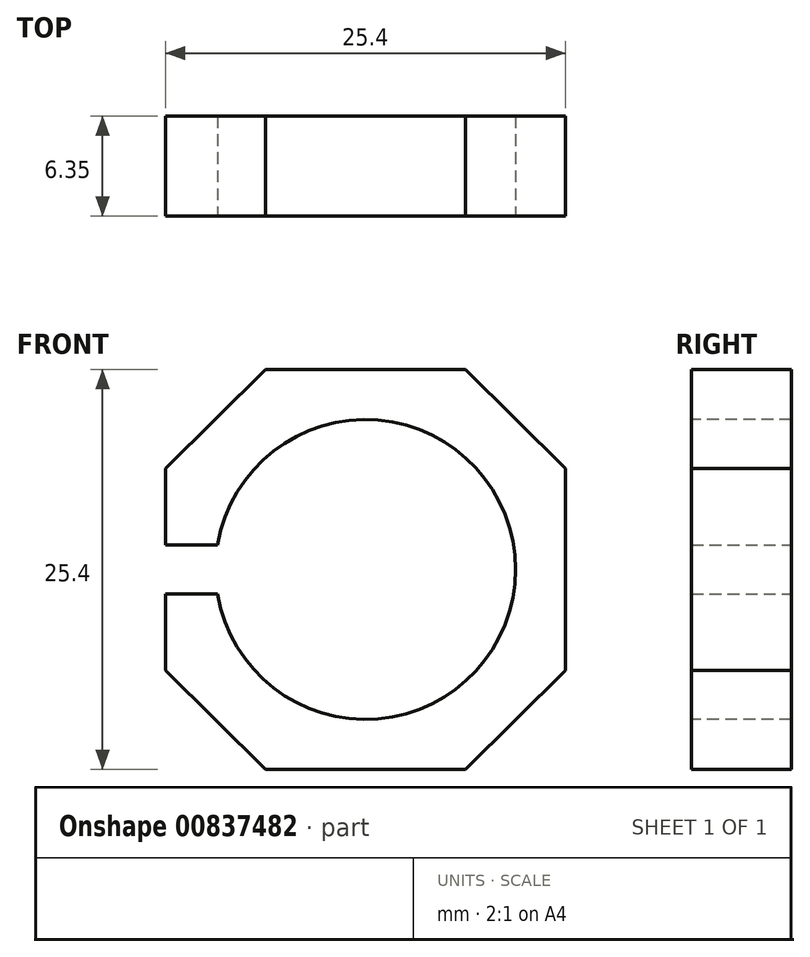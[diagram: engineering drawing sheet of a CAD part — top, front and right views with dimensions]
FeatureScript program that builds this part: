
annotation { "Feature Type Name" : "Feature", "Feature Type Description" : "" }
export const myFeature = defineFeature(function(context is Context, id is Id, definition is map)
    precondition{}
    {
        {
            var Q0;
            Q0=qCreatedBy(makeId("Front.planeOp"),FACE);
            var sketch = newSketch(context, id + "F0", { "sketchPlane" : qUnion([Q0])});
            skLineSegment(sketch, "E0.bottom", {"start": v(-12.7, 12.7) * mm, "end": v(12.7, 12.7) * mm});
            skLineSegment(sketch, "E0.top", {"start": v(-12.7, -12.7) * mm, "end": v(12.7, -12.7) * mm});
            skLineSegment(sketch, "E0.left", {"start": v(-12.7, 12.7) * mm, "end": v(-12.7, -12.7) * mm});
            skLineSegment(sketch, "E0.right", {"start": v(12.7, 12.7) * mm, "end": v(12.7, -12.7) * mm});
            skPoint(sketch, "E0.middle", {"position": v(0, 0) * mm});
            skSolve(sketch);
        }
        {
            var Q0;
            Q0 = qSketchRegion(id + "F0", true);
            extrude(context, id + "F1", {"entities" : qUnion([Q0]), "oppositeDirection" : true, "depth" : 6.35 * mm, "offsetDistance" : 25.4 * mm});
        }
        {
            var Q0;
            Q0=makeQuery(id+"F1.opExtrude","CAP_FACE",FACE,{"disambiguationData":[OSD([sQuery(id+"F0.wireOp",EDGE,"E0.bottom"),sQuery(id+"F0.wireOp",EDGE,"E0.top"),sQuery(id+"F0.wireOp",EDGE,"E0.left"),sQuery(id+"F0.wireOp",EDGE,"E0.right")])],"isStart":true});
            var sketch = newSketch(context, id + "F2", { "sketchPlane" : qUnion([Q0])});
            skCircle(sketch, "E1", {"center": v(0, 0) * mm, "radius": 9.53 * mm});
            skSolve(sketch);
        }
        {
            var Q0;
            Q0 = qSketchRegion(id + "F2", true);
            extrude(context, id + "F3", {"entities" : qUnion([Q0]), "operationType" : NewBodyOperationType.REMOVE, "oppositeDirection" : true, "depth" : 6.35 * mm, "offsetDistance" : 25.4 * mm});
        }
        {
            var Q0;
            Q0=qCreatedBy(makeId("Front.planeOp"),FACE);
            var sketch = newSketch(context, id + "F4", { "sketchPlane" : qUnion([Q0])});
            skLineSegment(sketch, "E2", {"start": v(12.7, 12.7) * mm, "end": v(6.35, 12.7) * mm});
            skLineSegment(sketch, "E3", {"start": v(6.35, 12.7) * mm, "end": v(12.76, 6.35) * mm});
            skLineSegment(sketch, "E4", {"start": v(12.76, 6.35) * mm, "end": v(12.7, 12.7) * mm});
            skLineSegment(sketch, "E5.MirrorCS", {"start": v(-12.7, 12.7) * mm, "end": v(-6.35, 12.7) * mm});
            skLineSegment(sketch, "E6.MirrorCS", {"start": v(-12.76, 6.35) * mm, "end": v(-12.7, 12.7) * mm});
            skLineSegment(sketch, "E7.MirrorCS", {"start": v(-6.35, 12.7) * mm, "end": v(-12.76, 6.35) * mm});
            skLineSegment(sketch, "E8.MirrorCS", {"start": v(-12.7, -12.7) * mm, "end": v(-6.35, -12.7) * mm});
            skLineSegment(sketch, "E9.MirrorCS", {"start": v(-12.76, -6.35) * mm, "end": v(-12.7, -12.7) * mm});
            skLineSegment(sketch, "E10.MirrorCS", {"start": v(-6.35, -12.7) * mm, "end": v(-12.76, -6.35) * mm});
            skLineSegment(sketch, "E11.MirrorCS", {"start": v(12.7, -12.7) * mm, "end": v(6.35, -12.7) * mm});
            skLineSegment(sketch, "E12.MirrorCS", {"start": v(6.35, -12.7) * mm, "end": v(12.76, -6.35) * mm});
            skLineSegment(sketch, "E13.MirrorCS", {"start": v(12.76, -6.35) * mm, "end": v(12.7, -12.7) * mm});
            skSolve(sketch);
        }
        {
            var Q0;
            Q0 = qSketchRegion(id + "F4", true);
            extrude(context, id + "F5", {"entities" : qUnion([Q0]), "operationType" : NewBodyOperationType.REMOVE, "oppositeDirection" : true, "depth" : 6.35 * mm, "offsetDistance" : 25.4 * mm});
        }
        {
            var Q0;
            Q0=qCreatedBy(makeId("Front.planeOp"),FACE);
            var sketch = newSketch(context, id + "F6", { "sketchPlane" : qUnion([Q0])});
            skLineSegment(sketch, "E14.bottom", {"start": v(-6.91, 1.57) * mm, "end": v(-22.77, 1.57) * mm});
            skLineSegment(sketch, "E14.top", {"start": v(-6.91, -1.57) * mm, "end": v(-22.77, -1.57) * mm});
            skLineSegment(sketch, "E14.left", {"start": v(-6.91, 1.57) * mm, "end": v(-6.91, -1.57) * mm});
            skLineSegment(sketch, "E14.right", {"start": v(-22.77, 1.57) * mm, "end": v(-22.77, -1.57) * mm});
            skPoint(sketch, "E14.middle", {"position": v(-14.84, 0) * mm});
            skSolve(sketch);
        }
        {
            var Q0;
            Q0 = qSketchRegion(id + "F6", true);
            extrude(context, id + "F7", {"entities" : qUnion([Q0]), "operationType" : NewBodyOperationType.REMOVE, "oppositeDirection" : true, "depth" : 6.35 * mm, "offsetDistance" : 25.4 * mm});
        }
    });
